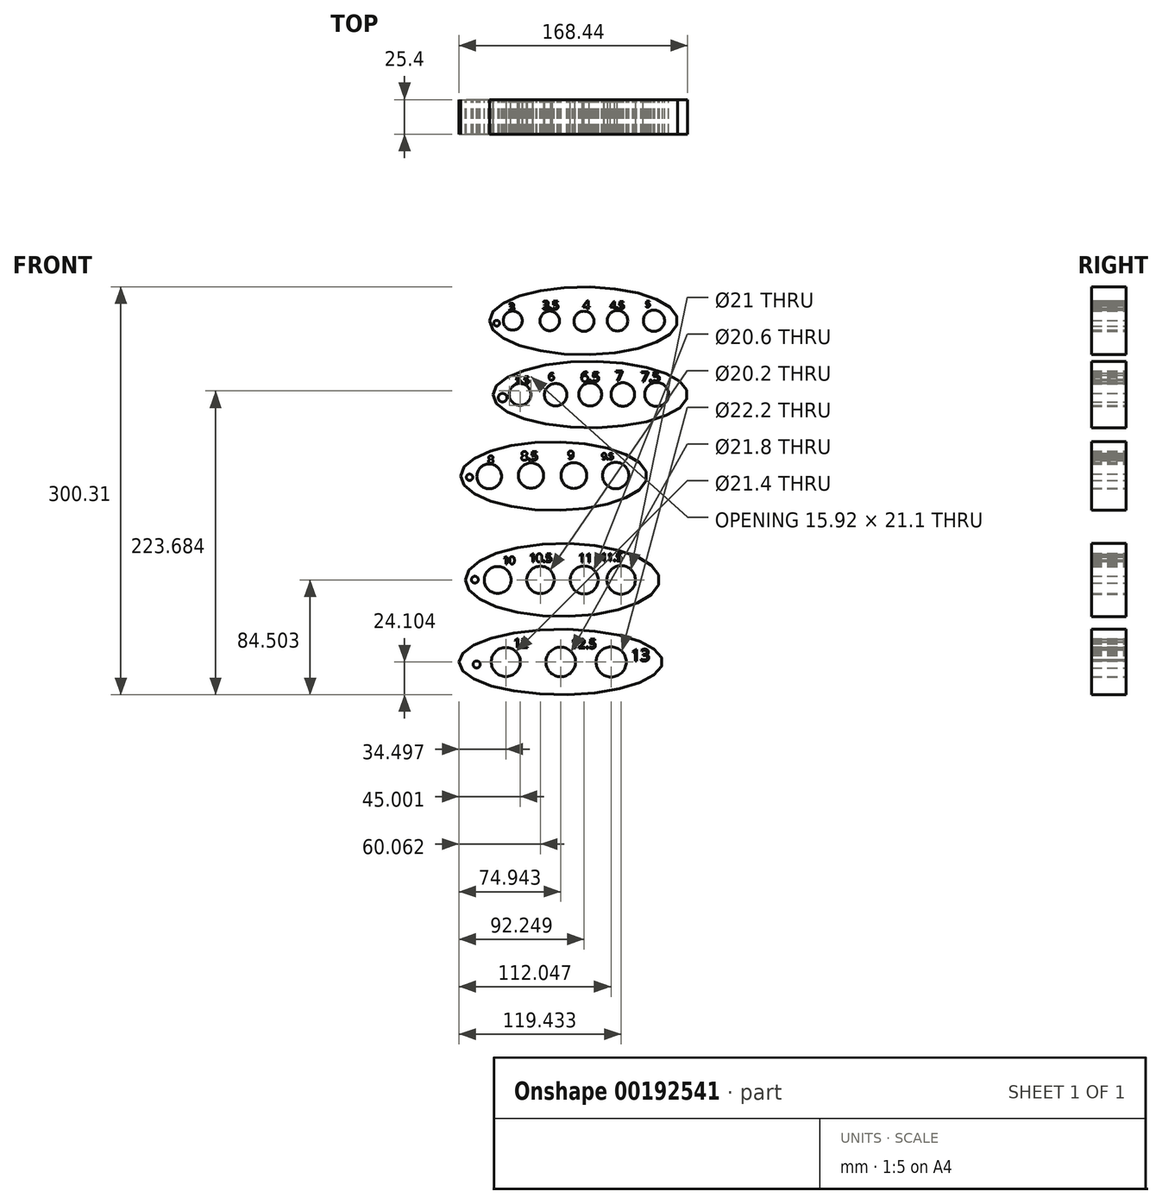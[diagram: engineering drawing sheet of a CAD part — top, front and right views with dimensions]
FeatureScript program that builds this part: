
annotation { "Feature Type Name" : "Feature", "Feature Type Description" : "" }
export const myFeature = defineFeature(function(context is Context, id is Id, definition is map)
    precondition{}
    {
        {
            var Q0;
            Q0=qCreatedBy(makeId("Front.planeOp"),FACE);
            var sketch = newSketch(context, id + "F0", { "sketchPlane" : qUnion([Q0])});
            skCircle(sketch, "E0", {"center": v(-57.14, 49.74) * mm, "radius": 7 * mm});
            skCircle(sketch, "E1", {"center": v(-29.91, 49.49) * mm, "radius": 7.2 * mm});
            skCircle(sketch, "E2", {"center": v(-4.7, 49.24) * mm, "radius": 7.4 * mm});
            skCircle(sketch, "E3", {"center": v(19.98, 49.62) * mm, "radius": 7.6 * mm});
            skCircle(sketch, "E4", {"center": v(46.81, 49.62) * mm, "radius": 7.8 * mm});
            skCircle(sketch, "E5", {"center": v(-51.75, -4.64) * mm, "radius": 8 * mm});
            skCircle(sketch, "E6", {"center": v(-25.54, -4.87) * mm, "radius": 8.22 * mm});
            skCircle(sketch, "E7", {"center": v(-0.13, -4.67) * mm, "radius": 8.45 * mm});
            skCircle(sketch, "E8", {"center": v(23.95, -4.67) * mm, "radius": 8.65 * mm});
            skCircle(sketch, "E9", {"center": v(48.85, -4.67) * mm, "radius": 8.85 * mm});
            skCircle(sketch, "E10", {"center": v(-74.47, -65) * mm, "radius": 9.1 * mm});
            skCircle(sketch, "E11", {"center": v(-43.65, -64.37) * mm, "radius": 9.3 * mm});
            skCircle(sketch, "E12", {"center": v(-12.13, -64.37) * mm, "radius": 9.5 * mm});
            skCircle(sketch, "E13", {"center": v(18.66, -64.37) * mm, "radius": 9.7 * mm});
            skCircle(sketch, "E14", {"center": v(-68.23, -141.27) * mm, "radius": 9.9 * mm});
            skCircle(sketch, "E15", {"center": v(-36.7, -141.27) * mm, "radius": 10.1 * mm});
            skCircle(sketch, "E16", {"center": v(-4.51, -141.27) * mm, "radius": 10.3 * mm});
            skCircle(sketch, "E17", {"center": v(22.67, -141.27) * mm, "radius": 10.5 * mm});
            skCircle(sketch, "E18", {"center": v(-62.26, -201.67) * mm, "radius": 10.7 * mm});
            skCircle(sketch, "E19", {"center": v(-21.82, -201.67) * mm, "radius": 10.9 * mm});
            skCircle(sketch, "E20", {"center": v(15.29, -201.67) * mm, "radius": 11.1 * mm});
            skEllipse(sketch, "E21", {"center": v(-5.02, 49.6) * mm, "majorRadius": 69.23 * mm, "minorRadius": 24.94 * mm, "majorAxis": v(-1, 0)});
            skPoint(sketch, "E22", {"position": v(-74.25, 49.6) * mm});
            skPoint(sketch, "E23", {"position": v(64.2, 49.6) * mm});
            skEllipse(sketch, "E24", {"center": v(0, -4.75) * mm, "majorRadius": 71.68 * mm, "minorRadius": 24.46 * mm, "majorAxis": v(-1, 0)});
            skEllipse(sketch, "E25", {"center": v(-26.93, -64.76) * mm, "majorRadius": 68.49 * mm, "minorRadius": 25.23 * mm, "majorAxis": v(-1, 0)});
            skEllipse(sketch, "E26", {"center": v(-20.62, -141.27) * mm, "majorRadius": 71.42 * mm, "minorRadius": 26.93 * mm, "majorAxis": v(-1, 0)});
            skEllipse(sketch, "E27", {"center": v(-21.82, -201.67) * mm, "majorRadius": 74.94 * mm, "minorRadius": 24.1 * mm, "majorAxis": v(-1, 0)});
            skText(sketch, "E28", { "text": "3\n", "fontName": "OpenSans-Regular.ttf"});
            skText(sketch, "E29", { "text": "3.5", "fontName": "OpenSans-Regular.ttf"});
            skText(sketch, "E30", { "text": "4", "fontName": "OpenSans-Regular.ttf"});
            skText(sketch, "E31", { "text": "4.5", "fontName": "OpenSans-Regular.ttf"});
            skText(sketch, "E32", { "text": "5", "fontName": "OpenSans-Regular.ttf"});
            skText(sketch, "E33", { "text": "5.5", "fontName": "OpenSans-Regular.ttf"});
            skText(sketch, "E34", { "text": "6.5", "fontName": "OpenSans-Regular.ttf"});
            skText(sketch, "E35", { "text": "6", "fontName": "OpenSans-Regular.ttf"});
            skText(sketch, "E36", { "text": "7", "fontName": "OpenSans-Regular.ttf"});
            skText(sketch, "E37", { "text": "7.5", "fontName": "OpenSans-Regular.ttf"});
            skText(sketch, "E38", { "text": "8", "fontName": "OpenSans-Regular.ttf"});
            skText(sketch, "E39", { "text": "8.5", "fontName": "OpenSans-Regular.ttf"});
            skText(sketch, "E40", { "text": "9", "fontName": "OpenSans-Regular.ttf"});
            skText(sketch, "E41", { "text": "9.5", "fontName": "OpenSans-Regular.ttf"});
            skText(sketch, "E42", { "text": "10", "fontName": "OpenSans-Regular.ttf"});
            skText(sketch, "E43", { "text": "10.5", "fontName": "OpenSans-Regular.ttf"});
            skText(sketch, "E44", { "text": "11", "fontName": "OpenSans-Regular.ttf"});
            skText(sketch, "E45", { "text": "11.5", "fontName": "OpenSans-Regular.ttf"});
            skText(sketch, "E46", { "text": "12", "fontName": "OpenSans-Regular.ttf"});
            skText(sketch, "E47", { "text": "12.5", "fontName": "OpenSans-Regular.ttf"});
            skText(sketch, "E48", { "text": "13", "fontName": "OpenSans-Regular.ttf"});
            skCircle(sketch, "E49", {"center": v(-83.72, -203.48) * mm, "radius": 2.6 * mm});
            skCircle(sketch, "E50", {"center": v(-85.02, -141.07) * mm, "radius": 2.53 * mm});
            skCircle(sketch, "E51", {"center": v(-88.92, -65.66) * mm, "radius": 2.33 * mm});
            skCircle(sketch, "E52", {"center": v(-64.59, -7.02) * mm, "radius": 3.15 * mm});
            skCircle(sketch, "E53", {"center": v(-68.94, 47.82) * mm, "radius": 2.14 * mm});
            const initialGuessF0  = {"E28": [-0.05995, 0.05718, 1, 0, 0.00532], "E29": [-0.03506, 0.05815, 1, 0, 0.00604], "E30": [-0.00538, 0.05815, 1, 0, 0.00628], "E31": [0.01471, 0.0584, 1, 0, 0.00532], "E32": [0.0406, 0.05976, 1, 0, 0.00444], "E33": [-0.0551, 0.00328, 1, 0, 0.00523], "E34": [-0.00699, 0.00485, 1, 0, 0.00706], "E35": [-0.03078, 0.0059, 1, 0, 0.00523], "E36": [0.01837, 0.00537, 1, 0, 0.00732], "E37": [0.0372, 0.00485, 1, 0, 0.00732], "E38": [-0.07537, -0.05518, 1, 0, 0.00529], "E39": [-0.05105, -0.05306, 1, 0, 0.00634], "E40": [-0.01658, -0.052, 1, 0, 0.0057], "E41": [0.00837, -0.05243, 1, 0, 0.00444], "E42": [-0.06405, -0.12945, 1, 0, 0.00537], "E43": [-0.0448, -0.12801, 1, 0, 0.00602], "E44": [-0.00864, -0.1283, 1, 0, 0.00631], "E45": [0.0079, -0.12725, 1, 0, 0.00563], "E46": [-0.05642, -0.19126, 1, 0, 0.00678], "E47": [-0.01418, -0.19158, 1, 0, 0.00671], "E48": [0.03002, -0.20088, 1, 0, 0.00861]};
            skSetInitialGuess(sketch, initialGuessF0);
            skSolve(sketch);
        }
        {
            var Q0;
            Q0=makeQuery(id+"F0.imprint","IMPRINT",FACE,{"disambiguationData":[TD([[makeQuery(id+"F0.imprint","IMPRINT",EDGE,{"derivedFrom":sQuery(id+"F0.wireOp",EDGE,"E0")}),-1.0]])]});
            var Q1;
            Q1=makeQuery(id+"F0.imprint","IMPRINT",FACE,{"disambiguationData":[TD([[makeQuery(id+"F0.imprint","IMPRINT",EDGE,{"derivedFrom":sQuery(id+"F0.wireOp",EDGE,"E6")}),-1.0]])]});
            var Q2;
            Q2=makeQuery(id+"F0.imprint","IMPRINT",FACE,{"disambiguationData":[TD([[makeQuery(id+"F0.imprint","IMPRINT",EDGE,{"derivedFrom":sQuery(id+"F0.wireOp",EDGE,"E10")}),-1.0]])]});
            var Q3;
            Q3=makeQuery(id+"F0.imprint","IMPRINT",FACE,{"disambiguationData":[TD([[makeQuery(id+"F0.imprint","IMPRINT",EDGE,{"derivedFrom":sQuery(id+"F0.wireOp",EDGE,"E14")}),-1.0]])]});
            var Q4;
            Q4=makeQuery(id+"F0.imprint","IMPRINT",FACE,{"disambiguationData":[TD([[makeQuery(id+"F0.imprint","IMPRINT",EDGE,{"derivedFrom":sQuery(id+"F0.wireOp",EDGE,"E18")}),-1.0]])]});
            extrude(context, id + "F1", {"entities" : qUnion([Q0, Q1, Q2, Q3, Q4]), "depth" : 25.4 * mm});
        }
    });
